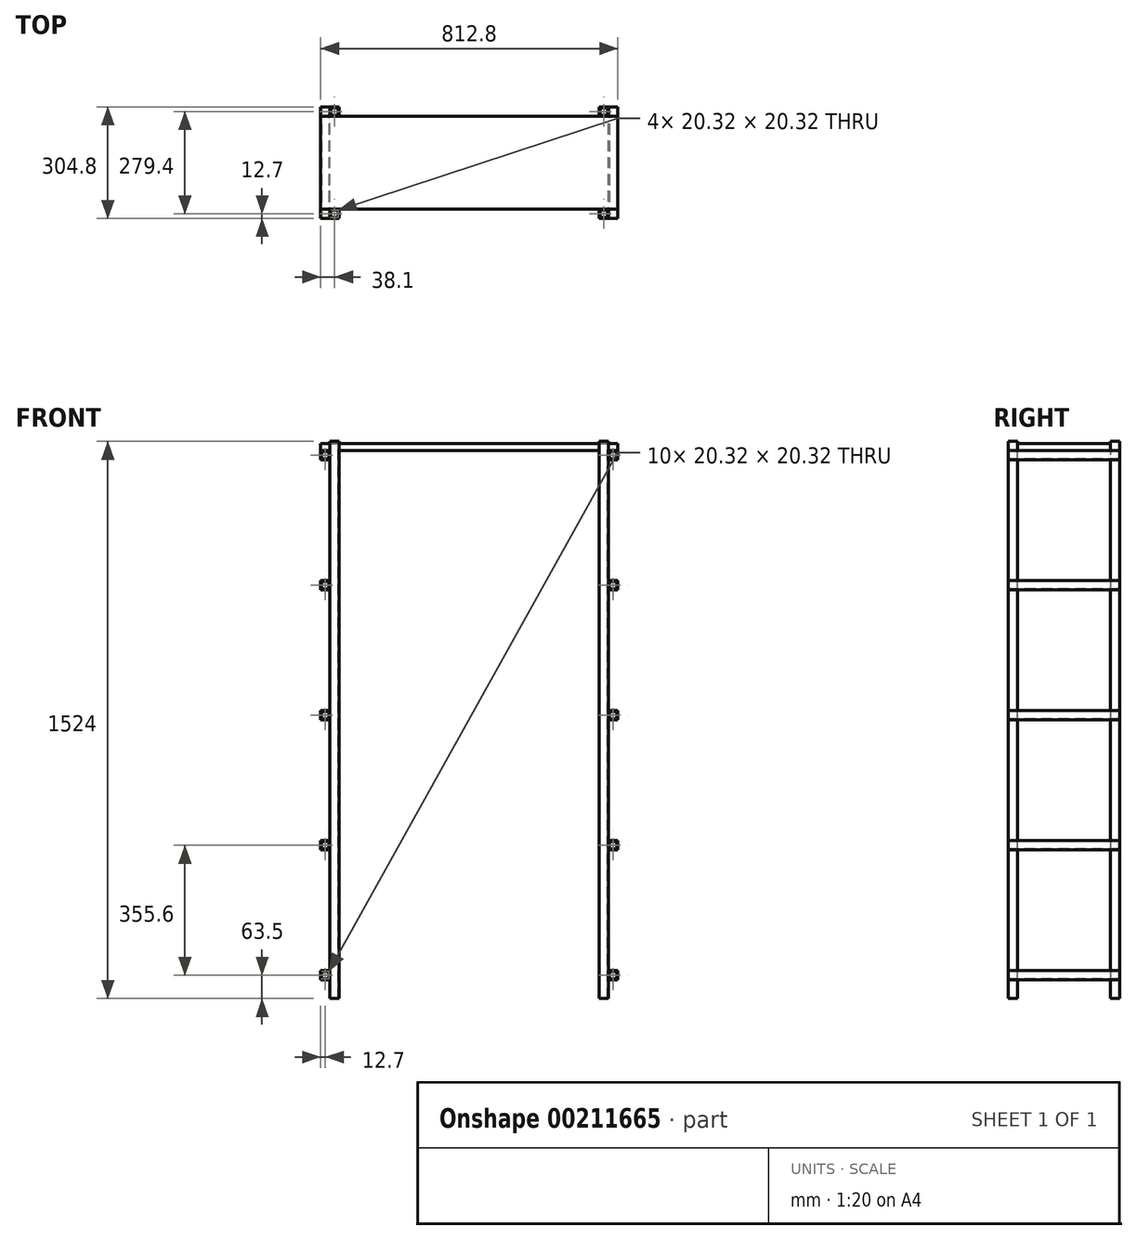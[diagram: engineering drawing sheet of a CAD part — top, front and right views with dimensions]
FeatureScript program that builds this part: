
annotation { "Feature Type Name" : "Feature", "Feature Type Description" : "" }
export const myFeature = defineFeature(function(context is Context, id is Id, definition is map)
    precondition{}
    {
        {
            var Q0;
            Q0=qCreatedBy(makeId("Right.planeOp"),FACE);
            var sketch = newSketch(context, id + "F0", { "sketchPlane" : qUnion([Q0])});
            skLineSegment(sketch, "E0.bottom", {"start": v(0, 0) * mm, "end": v(25.4, 0) * mm});
            skLineSegment(sketch, "E0.top", {"start": v(0, 1524) * mm, "end": v(25.4, 1524) * mm});
            skLineSegment(sketch, "E0.left", {"start": v(0, 0) * mm, "end": v(0, 1524) * mm});
            skLineSegment(sketch, "E0.right", {"start": v(25.4, 0) * mm, "end": v(25.4, 1524) * mm});
            skLineSegment(sketch, "E1.right", {"start": v(279.4, 1524) * mm, "end": v(279.4, 1498.6) * mm});
            skLineSegment(sketch, "E2.bottom", {"start": v(279.4, 1524) * mm, "end": v(304.8, 1524) * mm});
            skLineSegment(sketch, "E2.top", {"start": v(279.4, 0) * mm, "end": v(304.8, 0) * mm});
            skLineSegment(sketch, "E2.left", {"start": v(279.4, 1498.6) * mm, "end": v(279.4, 0) * mm});
            skLineSegment(sketch, "E2.right", {"start": v(304.8, 1524) * mm, "end": v(304.8, 0) * mm});
            skSolve(sketch);
        }
        {
            var Q0;
            Q0=makeQuery(id+"F0.imprint","IMPRINT",FACE,{"disambiguationData":[TD([[makeQuery(id+"F0.imprint","IMPRINT",EDGE,{"derivedFrom":sQuery(id+"F0.wireOp",EDGE,"E0.bottom")}),1.0]])]});
            var Q1;
            Q1=makeQuery(id+"F0.imprint","IMPRINT",FACE,{"disambiguationData":[TD([[makeQuery(id+"F0.imprint","IMPRINT",EDGE,{"derivedFrom":sQuery(id+"F0.wireOp",EDGE,"E1.right")}),1.0]])]});
            extrude(context, id + "F1", {"entities" : qUnion([Q0, Q1]), "depth" : 25.4 * mm});
        }
        {
            var Q0;
            Q0=makeQuery(id+"F1.opExtrude","CAP_FACE",FACE,{"disambiguationData":[OSD([sQuery(id+"F0.wireOp",EDGE,"E0.bottom"),sQuery(id+"F0.wireOp",EDGE,"E0.top"),sQuery(id+"F0.wireOp",EDGE,"E0.left"),sQuery(id+"F0.wireOp",EDGE,"E0.right")])],"isStart":false});
            var sketch = newSketch(context, id + "F2", { "sketchPlane" : qUnion([Q0])});
            skLineSegment(sketch, "E3", {"start": v(0, 1524) * mm, "end": v(0, 1498.6) * mm});
            skLineSegment(sketch, "E4.bottom", {"start": v(0, 1498.6) * mm, "end": v(304.8, 1498.6) * mm});
            skLineSegment(sketch, "E4.top", {"start": v(0, 1473.2) * mm, "end": v(304.8, 1473.2) * mm});
            skLineSegment(sketch, "E4.left", {"start": v(0, 1498.6) * mm, "end": v(0, 1473.2) * mm});
            skLineSegment(sketch, "E4.right", {"start": v(304.8, 1498.6) * mm, "end": v(304.8, 1473.2) * mm});
            skLineSegment(sketch, "E5", {"start": v(0, 1473.2) * mm, "end": v(0, 1143) * mm});
            skLineSegment(sketch, "E6.bottom", {"start": v(0, 1143) * mm, "end": v(304.8, 1143) * mm});
            skLineSegment(sketch, "E6.top", {"start": v(0, 1117.6) * mm, "end": v(304.8, 1117.6) * mm});
            skLineSegment(sketch, "E6.left", {"start": v(0, 1143) * mm, "end": v(0, 1117.6) * mm});
            skLineSegment(sketch, "E6.right", {"start": v(304.8, 1143) * mm, "end": v(304.8, 1117.6) * mm});
            skLineSegment(sketch, "E7", {"start": v(0, 1117.6) * mm, "end": v(0, 787.4) * mm});
            skLineSegment(sketch, "E8.bottom", {"start": v(0, 787.4) * mm, "end": v(304.8, 787.4) * mm});
            skLineSegment(sketch, "E8.top", {"start": v(0, 762) * mm, "end": v(304.8, 762) * mm});
            skLineSegment(sketch, "E8.left", {"start": v(0, 787.4) * mm, "end": v(0, 762) * mm});
            skLineSegment(sketch, "E8.right", {"start": v(304.8, 787.4) * mm, "end": v(304.8, 762) * mm});
            skLineSegment(sketch, "E9", {"start": v(0, 762) * mm, "end": v(0, 431.8) * mm});
            skLineSegment(sketch, "E10.bottom", {"start": v(0, 431.8) * mm, "end": v(304.8, 431.8) * mm});
            skLineSegment(sketch, "E10.top", {"start": v(0, 406.4) * mm, "end": v(304.8, 406.4) * mm});
            skLineSegment(sketch, "E10.left", {"start": v(0, 431.8) * mm, "end": v(0, 406.4) * mm});
            skLineSegment(sketch, "E10.right", {"start": v(304.8, 431.8) * mm, "end": v(304.8, 406.4) * mm});
            skLineSegment(sketch, "E11", {"start": v(0, 406.4) * mm, "end": v(0, 76.2) * mm});
            skLineSegment(sketch, "E12.bottom", {"start": v(0, 76.2) * mm, "end": v(304.8, 76.2) * mm});
            skLineSegment(sketch, "E12.top", {"start": v(0, 50.8) * mm, "end": v(304.8, 50.8) * mm});
            skLineSegment(sketch, "E12.left", {"start": v(0, 76.2) * mm, "end": v(0, 50.8) * mm});
            skLineSegment(sketch, "E12.right", {"start": v(304.8, 76.2) * mm, "end": v(304.8, 50.8) * mm});
            skSolve(sketch);
        }
        {
            var Q0;
            Q0=qCreatedBy(makeId("Right.planeOp"),FACE);
            cPlane(context, id + "F3", {"entities" : qUnion([Q0]), "cplaneType" : CPlaneType.OFFSET, "offset" : 355.6 * mm, "oppositeDirection" : true, "width" : 152.4 * mm, "height" : 152.4 * mm});
        }
        {
            var Q0;
            {var subQ0=sQuery(id+"F2.wireOp",EDGE,"E4.right");Q0=makeQuery(id+"F2.imprint","IMPRINT",FACE,{"disambiguationData":[TD([[makeQuery(id+"F2.imprint","IMPRINT",EDGE,{"derivedFrom":subQ0}),-1.0]])]});}
            var Q1;
            {var subQ0=sQuery(id+"F2.wireOp",EDGE,"E6.right");Q1=makeQuery(id+"F2.imprint","IMPRINT",FACE,{"disambiguationData":[TD([[makeQuery(id+"F2.imprint","IMPRINT",EDGE,{"derivedFrom":subQ0}),-1.0]])]});}
            var Q2;
            {var subQ0=sQuery(id+"F2.wireOp",EDGE,"E8.right");Q2=makeQuery(id+"F2.imprint","IMPRINT",FACE,{"disambiguationData":[TD([[makeQuery(id+"F2.imprint","IMPRINT",EDGE,{"derivedFrom":subQ0}),-1.0]])]});}
            var Q3;
            {var subQ0=sQuery(id+"F2.wireOp",EDGE,"E10.right");Q3=makeQuery(id+"F2.imprint","IMPRINT",FACE,{"disambiguationData":[TD([[makeQuery(id+"F2.imprint","IMPRINT",EDGE,{"derivedFrom":subQ0}),-1.0]])]});}
            var Q4;
            {var subQ0=sQuery(id+"F2.wireOp",EDGE,"E12.right");Q4=makeQuery(id+"F2.imprint","IMPRINT",FACE,{"disambiguationData":[TD([[makeQuery(id+"F2.imprint","IMPRINT",EDGE,{"derivedFrom":subQ0}),-1.0]])]});}
            var Q5;
            {var subQ0=sQuery(id+"F2.wireOp",EDGE,"E6.left");Q5=makeQuery(id+"F2.imprint","IMPRINT",FACE,{"disambiguationData":[TD([[makeQuery(id+"F2.imprint","IMPRINT",EDGE,{"derivedFrom":subQ0}),-1.0]])]});}
            var Q6;
            {var subQ0=sQuery(id+"F2.wireOp",EDGE,"E8.left");Q6=makeQuery(id+"F2.imprint","IMPRINT",FACE,{"disambiguationData":[TD([[makeQuery(id+"F2.imprint","IMPRINT",EDGE,{"derivedFrom":subQ0}),-1.0]])]});}
            var Q7;
            {var subQ0=sQuery(id+"F2.wireOp",EDGE,"E10.left");Q7=makeQuery(id+"F2.imprint","IMPRINT",FACE,{"disambiguationData":[TD([[makeQuery(id+"F2.imprint","IMPRINT",EDGE,{"derivedFrom":subQ0}),-1.0]])]});}
            var Q8;
            {var subQ0=sQuery(id+"F2.wireOp",EDGE,"E12.left");Q8=makeQuery(id+"F2.imprint","IMPRINT",FACE,{"disambiguationData":[TD([[makeQuery(id+"F2.imprint","IMPRINT",EDGE,{"derivedFrom":subQ0}),-1.0]])]});}
            var Q9;
            {var subQ0=sQuery(id+"F2.wireOp",EDGE,"E4.left");Q9=makeQuery(id+"F2.imprint","IMPRINT",FACE,{"disambiguationData":[TD([[makeQuery(id+"F2.imprint","IMPRINT",EDGE,{"derivedFrom":subQ0}),-1.0]])]});}
            extrude(context, id + "F4", {"entities" : qUnion([Q0, Q1, Q2, Q3, Q4, Q5, Q6, Q7, Q8, Q9]), "depth" : 25.4 * mm});
        }
        {
            var Q0;
            Q0=makeQuery(id+"F1.opExtrude","SWEPT_BODY",BODY,{"disambiguationData":[OSD([sQuery(id+"F0.wireOp",EDGE,"E0.bottom"),sQuery(id+"F0.wireOp",EDGE,"E0.top"),sQuery(id+"F0.wireOp",EDGE,"E0.left"),sQuery(id+"F0.wireOp",EDGE,"E0.right")])]});
            var Q1;
            Q1=makeQuery(id+"F4.opExtrude","SWEPT_BODY",BODY,{"disambiguationData":[OSD([sQuery(id+"F2.wireOp",EDGE,"E4.bottom"),sQuery(id+"F2.wireOp",EDGE,"E4.top"),sQuery(id+"F2.wireOp",EDGE,"E4.left"),sQuery(id+"F2.wireOp",EDGE,"E4.right")])]});
            var Q2;
            Q2=makeQuery(id+"F1.opExtrude","SWEPT_BODY",BODY,{"disambiguationData":[OSD([sQuery(id+"F0.wireOp",EDGE,"E1.right"),sQuery(id+"F0.wireOp",EDGE,"E2.bottom"),sQuery(id+"F0.wireOp",EDGE,"E2.top"),sQuery(id+"F0.wireOp",EDGE,"E2.left"),sQuery(id+"F0.wireOp",EDGE,"E2.right")])]});
            var Q3;
            Q3=makeQuery(id+"F4.opExtrude","SWEPT_BODY",BODY,{"disambiguationData":[OSD([sQuery(id+"F2.wireOp",EDGE,"E12.bottom"),sQuery(id+"F2.wireOp",EDGE,"E12.top"),sQuery(id+"F2.wireOp",EDGE,"E12.left"),sQuery(id+"F2.wireOp",EDGE,"E12.right")])]});
            var Q4;
            Q4=makeQuery(id+"F4.opExtrude","SWEPT_BODY",BODY,{"disambiguationData":[OSD([sQuery(id+"F2.wireOp",EDGE,"E6.bottom"),sQuery(id+"F2.wireOp",EDGE,"E6.top"),sQuery(id+"F2.wireOp",EDGE,"E6.left"),sQuery(id+"F2.wireOp",EDGE,"E6.right")])]});
            var Q5;
            Q5=makeQuery(id+"F4.opExtrude","SWEPT_BODY",BODY,{"disambiguationData":[OSD([sQuery(id+"F2.wireOp",EDGE,"E10.bottom"),sQuery(id+"F2.wireOp",EDGE,"E10.top"),sQuery(id+"F2.wireOp",EDGE,"E10.left"),sQuery(id+"F2.wireOp",EDGE,"E10.right")])]});
            var Q6;
            Q6=makeQuery(id+"F4.opExtrude","SWEPT_BODY",BODY,{"disambiguationData":[OSD([sQuery(id+"F2.wireOp",EDGE,"E8.bottom"),sQuery(id+"F2.wireOp",EDGE,"E8.top"),sQuery(id+"F2.wireOp",EDGE,"E8.left"),sQuery(id+"F2.wireOp",EDGE,"E8.right")])]});
            var Q7;
            Q7=qCreatedBy(id+"F3.planeOp",FACE);
            mirror(context, id + "F5", {"entities" : qUnion([Q0, Q1, Q2, Q3, Q4, Q5, Q6]), "mirrorPlane" : qUnion([Q7])});
        }
        {
            var Q0;
            Q0=makeQuery(id+"F4.opExtrude","CAP_FACE",FACE,{"disambiguationData":[OSD([sQuery(id+"F2.wireOp",EDGE,"E4.bottom"),sQuery(id+"F2.wireOp",EDGE,"E4.top"),sQuery(id+"F2.wireOp",EDGE,"E4.left"),sQuery(id+"F2.wireOp",EDGE,"E4.right")])],"isStart":false});
            var sketch = newSketch(context, id + "F6", { "sketchPlane" : qUnion([Q0])});
            skLineSegment(sketch, "E13.0", {"start": v(25.4, 0) * mm, "end": v(25.4, 1524) * mm});
            skLineSegment(sketch, "E14.bottom", {"start": v(25.4, 1498.6) * mm, "end": v(279.4, 1498.6) * mm});
            skLineSegment(sketch, "E14.top", {"start": v(25.4, 1517.65) * mm, "end": v(279.4, 1517.65) * mm});
            skLineSegment(sketch, "E14.left", {"start": v(25.4, 1498.6) * mm, "end": v(25.4, 1517.65) * mm});
            skLineSegment(sketch, "E14.right", {"start": v(279.4, 1498.6) * mm, "end": v(279.4, 1517.65) * mm});
            skLineSegment(sketch, "E15.0", {"start": v(0, 1143) * mm, "end": v(304.8, 1143) * mm});
            skLineSegment(sketch, "E16.bottom", {"start": v(25.4, 1143) * mm, "end": v(279.4, 1143) * mm});
            skLineSegment(sketch, "E16.top", {"start": v(25.4, 1162.05) * mm, "end": v(279.4, 1162.05) * mm});
            skLineSegment(sketch, "E16.left", {"start": v(25.4, 1143) * mm, "end": v(25.4, 1162.05) * mm});
            skLineSegment(sketch, "E16.right", {"start": v(279.4, 1143) * mm, "end": v(279.4, 1162.05) * mm});
            skLineSegment(sketch, "E17.0", {"start": v(0, 787.4) * mm, "end": v(304.8, 787.4) * mm});
            skLineSegment(sketch, "E18.bottom", {"start": v(25.4, 787.4) * mm, "end": v(279.4, 787.4) * mm});
            skLineSegment(sketch, "E18.top", {"start": v(25.4, 806.45) * mm, "end": v(279.4, 806.45) * mm});
            skLineSegment(sketch, "E18.left", {"start": v(25.4, 787.4) * mm, "end": v(25.4, 806.45) * mm});
            skLineSegment(sketch, "E18.right", {"start": v(279.4, 787.4) * mm, "end": v(279.4, 806.45) * mm});
            skLineSegment(sketch, "E19.0", {"start": v(0, 431.8) * mm, "end": v(304.8, 431.8) * mm});
            skLineSegment(sketch, "E20.0", {"start": v(0, 76.2) * mm, "end": v(304.8, 76.2) * mm});
            skLineSegment(sketch, "E21.bottom", {"start": v(25.4, 431.8) * mm, "end": v(279.4, 431.8) * mm});
            skLineSegment(sketch, "E21.top", {"start": v(25.4, 450.85) * mm, "end": v(279.4, 450.85) * mm});
            skLineSegment(sketch, "E21.left", {"start": v(25.4, 431.8) * mm, "end": v(25.4, 450.85) * mm});
            skLineSegment(sketch, "E21.right", {"start": v(279.4, 431.8) * mm, "end": v(279.4, 450.85) * mm});
            skLineSegment(sketch, "E22.bottom", {"start": v(25.4, 76.2) * mm, "end": v(279.4, 76.2) * mm});
            skLineSegment(sketch, "E22.top", {"start": v(25.4, 95.25) * mm, "end": v(279.4, 95.25) * mm});
            skLineSegment(sketch, "E22.left", {"start": v(25.4, 76.2) * mm, "end": v(25.4, 95.25) * mm});
            skLineSegment(sketch, "E22.right", {"start": v(279.4, 76.2) * mm, "end": v(279.4, 95.25) * mm});
            skSolve(sketch);
        }
        {
            var Q0;
            Q0=makeQuery(id+"F6.imprint","IMPRINT",FACE,{"disambiguationData":[TD([[makeQuery(id+"F6.imprint","IMPRINT",EDGE,{"derivedFrom":sQuery(id+"F6.wireOp",EDGE,"E14.bottom")}),1.0]])]});
            var Q1;
            Q1=makeQuery(id+"F6.imprint","IMPRINT",FACE,{"disambiguationData":[TD([[makeQuery(id+"F6.imprint","IMPRINT",EDGE,{"derivedFrom":sQuery(id+"F6.wireOp",EDGE,"E16.bottom")}),1.0]])]});
            var Q2;
            Q2=makeQuery(id+"F6.imprint","IMPRINT",FACE,{"disambiguationData":[TD([[makeQuery(id+"F6.imprint","IMPRINT",EDGE,{"derivedFrom":sQuery(id+"F6.wireOp",EDGE,"E18.bottom")}),1.0]])]});
            var Q3;
            Q3=makeQuery(id+"F6.imprint","IMPRINT",FACE,{"disambiguationData":[TD([[makeQuery(id+"F6.imprint","IMPRINT",EDGE,{"derivedFrom":sQuery(id+"F6.wireOp",EDGE,"E21.bottom")}),1.0]])]});
            var Q4;
            Q4=makeQuery(id+"F6.imprint","IMPRINT",FACE,{"disambiguationData":[TD([[makeQuery(id+"F6.imprint","IMPRINT",EDGE,{"derivedFrom":sQuery(id+"F6.wireOp",EDGE,"E22.bottom")}),1.0]])]});
            extrude(context, id + "F7", {"entities" : qUnion([Q0, Q1, Q2, Q3, Q4]), "oppositeDirection" : true, "depth" : 812.8 * mm});
        }
        {
            var Q0;
            Q0=makeQuery(id+"F4.opExtrude","SWEPT_FACE",FACE,{"disambiguationData":[OSD([sQuery(id+"F2.wireOp",EDGE,"E8.left")])]});
            var sketch = newSketch(context, id + "F8", { "sketchPlane" : qUnion([Q0])});
            skLineSegment(sketch, "E23.0.0", {"start": v(25.4, 76.2) * mm, "end": v(25.4, 50.8) * mm});
            skLineSegment(sketch, "E23.0.1", {"start": v(25.4, 50.8) * mm, "end": v(50.8, 50.8) * mm});
            skLineSegment(sketch, "E23.0.2", {"start": v(50.8, 50.8) * mm, "end": v(50.8, 76.2) * mm});
            skLineSegment(sketch, "E23.0.3", {"start": v(50.8, 76.2) * mm, "end": v(25.4, 76.2) * mm});
            skLineSegment(sketch, "E24.0.0", {"start": v(25.4, 431.8) * mm, "end": v(25.4, 406.4) * mm});
            skLineSegment(sketch, "E24.0.1", {"start": v(25.4, 406.4) * mm, "end": v(50.8, 406.4) * mm});
            skLineSegment(sketch, "E24.0.2", {"start": v(50.8, 406.4) * mm, "end": v(50.8, 431.8) * mm});
            skLineSegment(sketch, "E24.0.3", {"start": v(50.8, 431.8) * mm, "end": v(25.4, 431.8) * mm});
            skLineSegment(sketch, "E25.0.0", {"start": v(25.4, 787.4) * mm, "end": v(25.4, 762) * mm});
            skLineSegment(sketch, "E25.0.1", {"start": v(25.4, 762) * mm, "end": v(50.8, 762) * mm});
            skLineSegment(sketch, "E25.0.2", {"start": v(50.8, 762) * mm, "end": v(50.8, 787.4) * mm});
            skLineSegment(sketch, "E25.0.3", {"start": v(50.8, 787.4) * mm, "end": v(25.4, 787.4) * mm});
            skLineSegment(sketch, "E26.0.0", {"start": v(-736.6, 50.8) * mm, "end": v(-736.6, 76.2) * mm});
            skLineSegment(sketch, "E26.0.1", {"start": v(-736.6, 76.2) * mm, "end": v(-762, 76.2) * mm});
            skLineSegment(sketch, "E26.0.2", {"start": v(-762, 76.2) * mm, "end": v(-762, 50.8) * mm});
            skLineSegment(sketch, "E26.0.3", {"start": v(-762, 50.8) * mm, "end": v(-736.6, 50.8) * mm});
            skLineSegment(sketch, "E27.0.0", {"start": v(-736.6, 406.4) * mm, "end": v(-736.6, 431.8) * mm});
            skLineSegment(sketch, "E27.0.1", {"start": v(-736.6, 431.8) * mm, "end": v(-762, 431.8) * mm});
            skLineSegment(sketch, "E27.0.2", {"start": v(-762, 431.8) * mm, "end": v(-762, 406.4) * mm});
            skLineSegment(sketch, "E27.0.3", {"start": v(-762, 406.4) * mm, "end": v(-736.6, 406.4) * mm});
            skLineSegment(sketch, "E28.0.0", {"start": v(-736.6, 762) * mm, "end": v(-736.6, 787.4) * mm});
            skLineSegment(sketch, "E28.0.1", {"start": v(-736.6, 787.4) * mm, "end": v(-762, 787.4) * mm});
            skLineSegment(sketch, "E28.0.2", {"start": v(-762, 787.4) * mm, "end": v(-762, 762) * mm});
            skLineSegment(sketch, "E28.0.3", {"start": v(-762, 762) * mm, "end": v(-736.6, 762) * mm});
            skLineSegment(sketch, "E29.0.0", {"start": v(25.4, 1498.6) * mm, "end": v(25.4, 1473.2) * mm});
            skLineSegment(sketch, "E29.0.1", {"start": v(25.4, 1473.2) * mm, "end": v(50.8, 1473.2) * mm});
            skLineSegment(sketch, "E29.0.2", {"start": v(50.8, 1473.2) * mm, "end": v(50.8, 1498.6) * mm});
            skLineSegment(sketch, "E29.0.3", {"start": v(50.8, 1498.6) * mm, "end": v(25.4, 1498.6) * mm});
            skLineSegment(sketch, "E30.0.0", {"start": v(25.4, 1143) * mm, "end": v(25.4, 1117.6) * mm});
            skLineSegment(sketch, "E30.0.1", {"start": v(25.4, 1117.6) * mm, "end": v(50.8, 1117.6) * mm});
            skLineSegment(sketch, "E30.0.2", {"start": v(50.8, 1117.6) * mm, "end": v(50.8, 1143) * mm});
            skLineSegment(sketch, "E30.0.3", {"start": v(50.8, 1143) * mm, "end": v(25.4, 1143) * mm});
            skLineSegment(sketch, "E31.0.0", {"start": v(-736.6, 1117.6) * mm, "end": v(-736.6, 1143) * mm});
            skLineSegment(sketch, "E31.0.1", {"start": v(-736.6, 1143) * mm, "end": v(-762, 1143) * mm});
            skLineSegment(sketch, "E31.0.2", {"start": v(-762, 1143) * mm, "end": v(-762, 1117.6) * mm});
            skLineSegment(sketch, "E31.0.3", {"start": v(-762, 1117.6) * mm, "end": v(-736.6, 1117.6) * mm});
            skLineSegment(sketch, "E32.0.0", {"start": v(-736.6, 1473.2) * mm, "end": v(-736.6, 1498.6) * mm});
            skLineSegment(sketch, "E32.0.1", {"start": v(-736.6, 1498.6) * mm, "end": v(-762, 1498.6) * mm});
            skLineSegment(sketch, "E32.0.2", {"start": v(-762, 1498.6) * mm, "end": v(-762, 1473.2) * mm});
            skLineSegment(sketch, "E32.0.3", {"start": v(-762, 1473.2) * mm, "end": v(-736.6, 1473.2) * mm});
            skLineSegment(sketch, "E33.0", {"start": v(27.94, 1496.06) * mm, "end": v(27.94, 1475.74) * mm});
            skLineSegment(sketch, "E33.1", {"start": v(48.26, 1496.06) * mm, "end": v(27.94, 1496.06) * mm});
            skLineSegment(sketch, "E33.2", {"start": v(48.26, 1475.74) * mm, "end": v(48.26, 1496.06) * mm});
            skLineSegment(sketch, "E33.3", {"start": v(27.94, 1475.74) * mm, "end": v(48.26, 1475.74) * mm});
            skLineSegment(sketch, "E34.0", {"start": v(27.94, 1140.46) * mm, "end": v(27.94, 1120.14) * mm});
            skLineSegment(sketch, "E34.1", {"start": v(48.26, 1140.46) * mm, "end": v(27.94, 1140.46) * mm});
            skLineSegment(sketch, "E34.2", {"start": v(48.26, 1120.14) * mm, "end": v(48.26, 1140.46) * mm});
            skLineSegment(sketch, "E34.3", {"start": v(27.94, 1120.14) * mm, "end": v(48.26, 1120.14) * mm});
            skLineSegment(sketch, "E35.0", {"start": v(-739.14, 1475.74) * mm, "end": v(-739.14, 1496.06) * mm});
            skLineSegment(sketch, "E35.1", {"start": v(-759.46, 1475.74) * mm, "end": v(-739.14, 1475.74) * mm});
            skLineSegment(sketch, "E35.2", {"start": v(-759.46, 1496.06) * mm, "end": v(-759.46, 1475.74) * mm});
            skLineSegment(sketch, "E35.3", {"start": v(-739.14, 1496.06) * mm, "end": v(-759.46, 1496.06) * mm});
            skLineSegment(sketch, "E36.0", {"start": v(-739.14, 1120.14) * mm, "end": v(-739.14, 1140.46) * mm});
            skLineSegment(sketch, "E36.1", {"start": v(-759.46, 1120.14) * mm, "end": v(-739.14, 1120.14) * mm});
            skLineSegment(sketch, "E36.2", {"start": v(-759.46, 1140.46) * mm, "end": v(-759.46, 1120.14) * mm});
            skLineSegment(sketch, "E36.3", {"start": v(-739.14, 1140.46) * mm, "end": v(-759.46, 1140.46) * mm});
            skLineSegment(sketch, "E37.0", {"start": v(-739.14, 764.54) * mm, "end": v(-739.14, 784.86) * mm});
            skLineSegment(sketch, "E37.1", {"start": v(-759.46, 764.54) * mm, "end": v(-739.14, 764.54) * mm});
            skLineSegment(sketch, "E37.2", {"start": v(-759.46, 784.86) * mm, "end": v(-759.46, 764.54) * mm});
            skLineSegment(sketch, "E37.3", {"start": v(-739.14, 784.86) * mm, "end": v(-759.46, 784.86) * mm});
            skLineSegment(sketch, "E38.0", {"start": v(27.94, 784.86) * mm, "end": v(27.94, 764.54) * mm});
            skLineSegment(sketch, "E38.1", {"start": v(48.26, 784.86) * mm, "end": v(27.94, 784.86) * mm});
            skLineSegment(sketch, "E38.2", {"start": v(48.26, 764.54) * mm, "end": v(48.26, 784.86) * mm});
            skLineSegment(sketch, "E38.3", {"start": v(27.94, 764.54) * mm, "end": v(48.26, 764.54) * mm});
            skLineSegment(sketch, "E39.0", {"start": v(27.94, 429.26) * mm, "end": v(27.94, 408.94) * mm});
            skLineSegment(sketch, "E39.1", {"start": v(48.26, 429.26) * mm, "end": v(27.94, 429.26) * mm});
            skLineSegment(sketch, "E39.2", {"start": v(48.26, 408.94) * mm, "end": v(48.26, 429.26) * mm});
            skLineSegment(sketch, "E39.3", {"start": v(27.94, 408.94) * mm, "end": v(48.26, 408.94) * mm});
            skLineSegment(sketch, "E40.0", {"start": v(27.94, 73.66) * mm, "end": v(27.94, 53.34) * mm});
            skLineSegment(sketch, "E40.1", {"start": v(48.26, 73.66) * mm, "end": v(27.94, 73.66) * mm});
            skLineSegment(sketch, "E40.2", {"start": v(48.26, 53.34) * mm, "end": v(48.26, 73.66) * mm});
            skLineSegment(sketch, "E40.3", {"start": v(27.94, 53.34) * mm, "end": v(48.26, 53.34) * mm});
            skLineSegment(sketch, "E41.0", {"start": v(-739.14, 53.34) * mm, "end": v(-739.14, 73.66) * mm});
            skLineSegment(sketch, "E41.1", {"start": v(-759.46, 53.34) * mm, "end": v(-739.14, 53.34) * mm});
            skLineSegment(sketch, "E41.2", {"start": v(-759.46, 73.66) * mm, "end": v(-759.46, 53.34) * mm});
            skLineSegment(sketch, "E41.3", {"start": v(-739.14, 73.66) * mm, "end": v(-759.46, 73.66) * mm});
            skLineSegment(sketch, "E42.0", {"start": v(-739.14, 408.94) * mm, "end": v(-739.14, 429.26) * mm});
            skLineSegment(sketch, "E42.1", {"start": v(-759.46, 408.94) * mm, "end": v(-739.14, 408.94) * mm});
            skLineSegment(sketch, "E42.2", {"start": v(-759.46, 429.26) * mm, "end": v(-759.46, 408.94) * mm});
            skLineSegment(sketch, "E42.3", {"start": v(-739.14, 429.26) * mm, "end": v(-759.46, 429.26) * mm});
            skSolve(sketch);
        }
        {
            var Q0;
            Q0=makeQuery(id+"F8.imprint","IMPRINT",FACE,{"disambiguationData":[TD([[makeQuery(id+"F8.imprint","IMPRINT",EDGE,{"derivedFrom":sQuery(id+"F8.wireOp",EDGE,"E35.0")}),1.0]])]});
            var Q1;
            Q1=makeQuery(id+"F8.imprint","IMPRINT",FACE,{"disambiguationData":[TD([[makeQuery(id+"F8.imprint","IMPRINT",EDGE,{"derivedFrom":sQuery(id+"F8.wireOp",EDGE,"E36.0")}),1.0]])]});
            var Q2;
            Q2=makeQuery(id+"F8.imprint","IMPRINT",FACE,{"disambiguationData":[TD([[makeQuery(id+"F8.imprint","IMPRINT",EDGE,{"derivedFrom":sQuery(id+"F8.wireOp",EDGE,"E37.0")}),1.0]])]});
            var Q3;
            Q3=makeQuery(id+"F8.imprint","IMPRINT",FACE,{"disambiguationData":[TD([[makeQuery(id+"F8.imprint","IMPRINT",EDGE,{"derivedFrom":sQuery(id+"F8.wireOp",EDGE,"E42.0")}),1.0]])]});
            var Q4;
            Q4=makeQuery(id+"F8.imprint","IMPRINT",FACE,{"disambiguationData":[TD([[makeQuery(id+"F8.imprint","IMPRINT",EDGE,{"derivedFrom":sQuery(id+"F8.wireOp",EDGE,"E41.0")}),1.0]])]});
            var Q5;
            Q5=makeQuery(id+"F8.imprint","IMPRINT",FACE,{"disambiguationData":[TD([[makeQuery(id+"F8.imprint","IMPRINT",EDGE,{"derivedFrom":sQuery(id+"F8.wireOp",EDGE,"E40.0")}),1.0]])]});
            var Q6;
            Q6=makeQuery(id+"F8.imprint","IMPRINT",FACE,{"disambiguationData":[TD([[makeQuery(id+"F8.imprint","IMPRINT",EDGE,{"derivedFrom":sQuery(id+"F8.wireOp",EDGE,"E38.0")}),1.0]])]});
            var Q7;
            Q7=makeQuery(id+"F8.imprint","IMPRINT",FACE,{"disambiguationData":[TD([[makeQuery(id+"F8.imprint","IMPRINT",EDGE,{"derivedFrom":sQuery(id+"F8.wireOp",EDGE,"E39.0")}),1.0]])]});
            var Q8;
            Q8=makeQuery(id+"F8.imprint","IMPRINT",FACE,{"disambiguationData":[TD([[makeQuery(id+"F8.imprint","IMPRINT",EDGE,{"derivedFrom":sQuery(id+"F8.wireOp",EDGE,"E33.0")}),1.0]])]});
            var Q9;
            Q9=makeQuery(id+"F8.imprint","IMPRINT",FACE,{"disambiguationData":[TD([[makeQuery(id+"F8.imprint","IMPRINT",EDGE,{"derivedFrom":sQuery(id+"F8.wireOp",EDGE,"E34.0")}),1.0]])]});
            extrude(context, id + "F9", {"entities" : qUnion([Q0, Q1, Q2, Q3, Q4, Q5, Q6, Q7, Q8, Q9]), "operationType" : NewBodyOperationType.REMOVE, "oppositeDirection" : true, "depth" : 304.8 * mm});
        }
        {
            var Q0;
            Q0=makeQuery(id+"F1.opExtrude","SWEPT_FACE",FACE,{"disambiguationData":[OSD([sQuery(id+"F0.wireOp",EDGE,"E0.top")])]});
            var sketch = newSketch(context, id + "F10", { "sketchPlane" : qUnion([Q0])});
            skLineSegment(sketch, "E43.0.0", {"start": v(-711.2, 0) * mm, "end": v(-711.2, 25.4) * mm});
            skLineSegment(sketch, "E43.0.1", {"start": v(-711.2, 25.4) * mm, "end": v(-736.6, 25.4) * mm});
            skLineSegment(sketch, "E43.0.2", {"start": v(-736.6, 25.4) * mm, "end": v(-736.6, 0) * mm});
            skLineSegment(sketch, "E43.0.3", {"start": v(-736.6, 0) * mm, "end": v(-711.2, 0) * mm});
            skLineSegment(sketch, "E44.0.0", {"start": v(-711.2, 279.4) * mm, "end": v(-711.2, 304.8) * mm});
            skLineSegment(sketch, "E44.0.1", {"start": v(-711.2, 304.8) * mm, "end": v(-736.6, 304.8) * mm});
            skLineSegment(sketch, "E44.0.2", {"start": v(-736.6, 304.8) * mm, "end": v(-736.6, 279.4) * mm});
            skLineSegment(sketch, "E44.0.3", {"start": v(-736.6, 279.4) * mm, "end": v(-711.2, 279.4) * mm});
            skLineSegment(sketch, "E45.0.0", {"start": v(0, 304.8) * mm, "end": v(0, 279.4) * mm});
            skLineSegment(sketch, "E45.0.1", {"start": v(0, 279.4) * mm, "end": v(25.4, 279.4) * mm});
            skLineSegment(sketch, "E45.0.2", {"start": v(25.4, 279.4) * mm, "end": v(25.4, 304.8) * mm});
            skLineSegment(sketch, "E45.0.3", {"start": v(25.4, 304.8) * mm, "end": v(0, 304.8) * mm});
            skLineSegment(sketch, "E46.0.0", {"start": v(0, 25.4) * mm, "end": v(0, 0) * mm});
            skLineSegment(sketch, "E46.0.1", {"start": v(0, 0) * mm, "end": v(25.4, 0) * mm});
            skLineSegment(sketch, "E46.0.2", {"start": v(25.4, 0) * mm, "end": v(25.4, 25.4) * mm});
            skLineSegment(sketch, "E46.0.3", {"start": v(25.4, 25.4) * mm, "end": v(0, 25.4) * mm});
            skLineSegment(sketch, "E47.0", {"start": v(2.54, 22.86) * mm, "end": v(2.54, 2.54) * mm});
            skLineSegment(sketch, "E47.1", {"start": v(22.86, 22.86) * mm, "end": v(2.54, 22.86) * mm});
            skLineSegment(sketch, "E47.2", {"start": v(22.86, 2.54) * mm, "end": v(22.86, 22.86) * mm});
            skLineSegment(sketch, "E47.3", {"start": v(2.54, 2.54) * mm, "end": v(22.86, 2.54) * mm});
            skLineSegment(sketch, "E48.0", {"start": v(2.54, 302.26) * mm, "end": v(2.54, 281.94) * mm});
            skLineSegment(sketch, "E48.1", {"start": v(22.86, 302.26) * mm, "end": v(2.54, 302.26) * mm});
            skLineSegment(sketch, "E48.2", {"start": v(22.86, 281.94) * mm, "end": v(22.86, 302.26) * mm});
            skLineSegment(sketch, "E48.3", {"start": v(2.54, 281.94) * mm, "end": v(22.86, 281.94) * mm});
            skLineSegment(sketch, "E49.0", {"start": v(-713.74, 281.94) * mm, "end": v(-713.74, 302.26) * mm});
            skLineSegment(sketch, "E49.1", {"start": v(-734.06, 281.94) * mm, "end": v(-713.74, 281.94) * mm});
            skLineSegment(sketch, "E49.2", {"start": v(-734.06, 302.26) * mm, "end": v(-734.06, 281.94) * mm});
            skLineSegment(sketch, "E49.3", {"start": v(-713.74, 302.26) * mm, "end": v(-734.06, 302.26) * mm});
            skLineSegment(sketch, "E50.0", {"start": v(-713.74, 2.54) * mm, "end": v(-713.74, 22.86) * mm});
            skLineSegment(sketch, "E50.1", {"start": v(-734.06, 2.54) * mm, "end": v(-713.74, 2.54) * mm});
            skLineSegment(sketch, "E50.2", {"start": v(-734.06, 22.86) * mm, "end": v(-734.06, 2.54) * mm});
            skLineSegment(sketch, "E50.3", {"start": v(-713.74, 22.86) * mm, "end": v(-734.06, 22.86) * mm});
            skSolve(sketch);
        }
        {
            var Q0;
            Q0=makeQuery(id+"F10.imprint","IMPRINT",FACE,{"disambiguationData":[TD([[makeQuery(id+"F10.imprint","IMPRINT",EDGE,{"derivedFrom":sQuery(id+"F10.wireOp",EDGE,"E50.0")}),1.0]])]});
            var Q1;
            Q1=makeQuery(id+"F10.imprint","IMPRINT",FACE,{"disambiguationData":[TD([[makeQuery(id+"F10.imprint","IMPRINT",EDGE,{"derivedFrom":sQuery(id+"F10.wireOp",EDGE,"E49.0")}),1.0]])]});
            var Q2;
            Q2=makeQuery(id+"F10.imprint","IMPRINT",FACE,{"disambiguationData":[TD([[makeQuery(id+"F10.imprint","IMPRINT",EDGE,{"derivedFrom":sQuery(id+"F10.wireOp",EDGE,"E47.0")}),1.0]])]});
            var Q3;
            Q3=makeQuery(id+"F10.imprint","IMPRINT",FACE,{"disambiguationData":[TD([[makeQuery(id+"F10.imprint","IMPRINT",EDGE,{"derivedFrom":sQuery(id+"F10.wireOp",EDGE,"E48.0")}),1.0]])]});
            extrude(context, id + "F11", {"entities" : qUnion([Q0, Q1, Q2, Q3]), "operationType" : NewBodyOperationType.REMOVE, "oppositeDirection" : true, "depth" : 1524 * mm});
        }
    });
